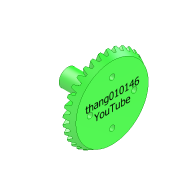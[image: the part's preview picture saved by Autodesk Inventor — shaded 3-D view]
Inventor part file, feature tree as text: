
AUTODESK INVENTOR PART (.ipt)
format: ipt  version: 2022.5 (Build 265521000, 521)  size: 528,896 bytes
history: native  units: in
note: dims shown in document units (in); Inventor stores cm internally (conversion verified against a paired STEP export)
features: sketch x8, extrude x5, plane x3, pattern_circular x3, revolve x1
ambient origin geometry x8: Origin, YZ Plane, XZ Plane, XY Plane, X Axis, Y Axis, Z Axis, Center Point
bodies: Solid1 (feature_tree)
feature tree (20):
  revolve  "Revolution1"  [1 undecoded]
  plane  "Work Plane7"
  extrude  "Extrusion7"  Depth=0.0787in
  plane  "Work Plane8"
  sketch  "Sketch13"  dims[d5=0.3937in d9=1.5748in]
  extrude  "Extrusion9"  Depth=1.5748in
  pattern_circular  "Circular Pattern4"  [2 undecoded]
  pattern_circular  "Circular Pattern5"  Count=4  [1 undecoded]
  extrude  "Extrusion10"  Depth=1.5748in
  extrude  "Extrusion11"  Depth=1.5748in
  sketch  "Sketch17"  dims[d76=0.9449in]
  extrude  "Extrusion12"  Depth=0.0787in
  pattern_circular  "Circular Pattern6"  [2 undecoded]
  sketch  "Sketch1"  dims[d0=3.1496in d1=0.1825in]
  plane  "Work Plane6"
  sketch  "Sketch11"  dims[d2=0.0787in d3=0.0945in]
  sketch  "Sketch14"  dims[d10=90.0deg]
  sketch  "Sketch15"  dims[d74=0.4359in]
  sketch  "Sketch16"  dims[d75=0.7087in]
  sketch  "Sketch18"  dims[d77=1.4085in d78=0.7043in d86=-0.1825in d87=1.5748in d88=0.0691in d89=0.1374in d90=0.0787in d91=0.0197in d92=0.0945in d93=0.0079in d94=0.0079in d95=0.4724in d96=-0.0197in d109=0.2406in d110=-0.2406in d111=2.8171in d112=1.3386in d113=0.4724in d114=0.5906in d115=0.0in d116=2.3622in d117=360.0deg d119=12.5984in d120=360.0deg d122=1.1811in d123=0.0787in d124=0.0in d125=0.6299in d126=1.2598in d127=0.0in d128=0.1969in d129=0.7874in d130=0.2362in d131=0.0in d132=1.5748in d133=360.0deg]
note: 6 required parameter values undecoded (feature->parameter linkage not recoverable at this tier; creation-order binding heuristic only, values carry confidence <= 0.55)